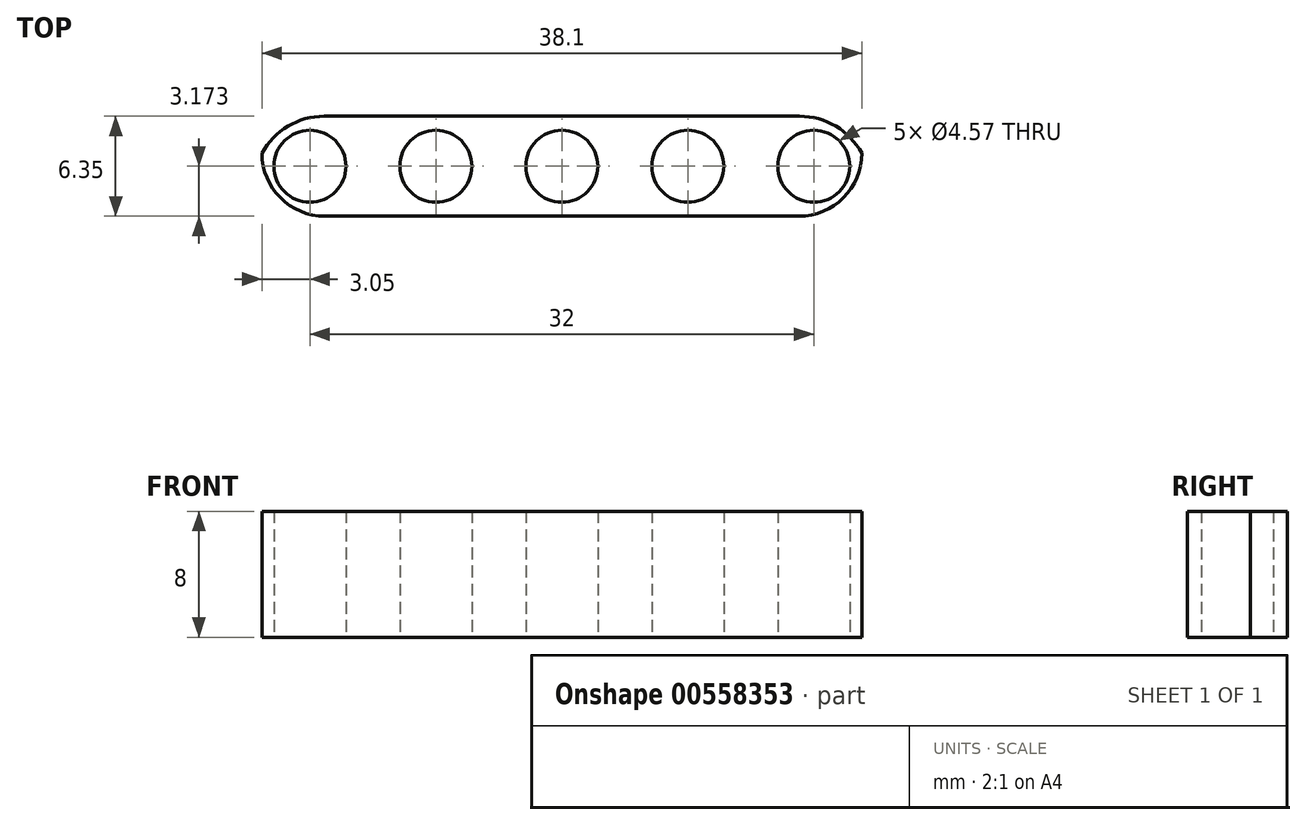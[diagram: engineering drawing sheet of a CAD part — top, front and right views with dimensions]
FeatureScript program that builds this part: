
annotation { "Feature Type Name" : "Feature", "Feature Type Description" : "" }
export const myFeature = defineFeature(function(context is Context, id is Id, definition is map)
    precondition{}
    {
        {
            var Q0;
            Q0=qCreatedBy(makeId("Top.planeOp"),FACE);
            var sketch = newSketch(context, id + "F0", { "sketchPlane" : qUnion([Q0])});
            skLineSegment(sketch, "E0", {"start": v(-18.9, 3.05) * mm, "end": v(19.2, 3.05) * mm});
            skLineSegment(sketch, "E1", {"start": v(19.2, 3.05) * mm, "end": v(19.2, -3.3) * mm});
            skLineSegment(sketch, "E2", {"start": v(19.2, -3.3) * mm, "end": v(-17.44, -3.3) * mm});
            skLineSegment(sketch, "E3", {"start": v(-18.9, 3.05) * mm, "end": v(-18.9, -3.33) * mm});
            skLineSegment(sketch, "E4", {"start": v(-18.9, -3.33) * mm, "end": v(-17.44, -3.3) * mm});
            skCircle(sketch, "E5", {"center": v(0.16, -0.13) * mm, "radius": 2.29 * mm});
            skCircle(sketch, "E6.1.0.0", {"center": v(8.16, -0.13) * mm, "radius": 2.29 * mm});
            skCircle(sketch, "E6.2.0.0", {"center": v(16.16, -0.13) * mm, "radius": 2.29 * mm});
            skLineSegment(sketch, "E6.direction1", {"start": v(0.16, -0.13) * mm, "end": v(8.16, -0.13) * mm, "construction": true});
            skCircle(sketch, "E7.1.0.0", {"center": v(-7.84, -0.13) * mm, "radius": 2.29 * mm});
            skCircle(sketch, "E7.2.0.0", {"center": v(-15.84, -0.13) * mm, "radius": 2.29 * mm});
            skLineSegment(sketch, "E7.direction1", {"start": v(0.16, -0.13) * mm, "end": v(-7.84, -0.13) * mm, "construction": true});
            skSolve(sketch);
        }
        {
            var Q0;
            Q0=makeQuery(id+"F0.imprint","IMPRINT",FACE,{"disambiguationData":[TD([[makeQuery(id+"F0.imprint","IMPRINT",EDGE,{"derivedFrom":sQuery(id+"F0.wireOp",EDGE,"E0")}),-1.0]])]});
            extrude(context, id + "F1", {"entities" : qUnion([Q0]), "depth" : 8 * mm, "offsetDistance" : 25.4 * mm});
        }
        {
            var Q0;
            Q0=makeQuery(id+"F1.opExtrude","SWEPT_EDGE",EDGE,{"disambiguationData":[OSD([sQuery(id+"F0.wireOp",EDGE,"E3"),sQuery(id+"F0.wireOp",EDGE,"E4")])]});
            fillet(context, id + "F2", {"entities" : qUnion([Q0]), "radius" : 4 * mm, "tangentPropagation" : true, "allowEdgeOverflow" : false});
        }
        {
            var Q0;
            Q0=makeQuery(id+"F1.opExtrude","SWEPT_EDGE",EDGE,{"disambiguationData":[OSD([sQuery(id+"F0.wireOp",EDGE,"E1"),sQuery(id+"F0.wireOp",EDGE,"E2")])]});
            fillet(context, id + "F3", {"entities" : qUnion([Q0]), "radius" : 4 * mm, "tangentPropagation" : true, "allowEdgeOverflow" : false});
        }
        {
            var Q0;
            Q0=makeQuery(id+"F1.opExtrude","SWEPT_EDGE",EDGE,{"disambiguationData":[OSD([sQuery(id+"F0.wireOp",EDGE,"E0"),sQuery(id+"F0.wireOp",EDGE,"E1")])]});
            fillet(context, id + "F4", {"entities" : qUnion([Q0]), "radius" : 4.5 * mm, "tangentPropagation" : true, "allowEdgeOverflow" : false});
        }
        {
            var Q0;
            Q0=makeQuery(id+"F1.opExtrude","SWEPT_EDGE",EDGE,{"disambiguationData":[OSD([sQuery(id+"F0.wireOp",EDGE,"E0"),sQuery(id+"F0.wireOp",EDGE,"E3")])]});
            fillet(context, id + "F5", {"entities" : qUnion([Q0]), "radius" : 4.5 * mm, "tangentPropagation" : true, "allowEdgeOverflow" : false});
        }
    });
